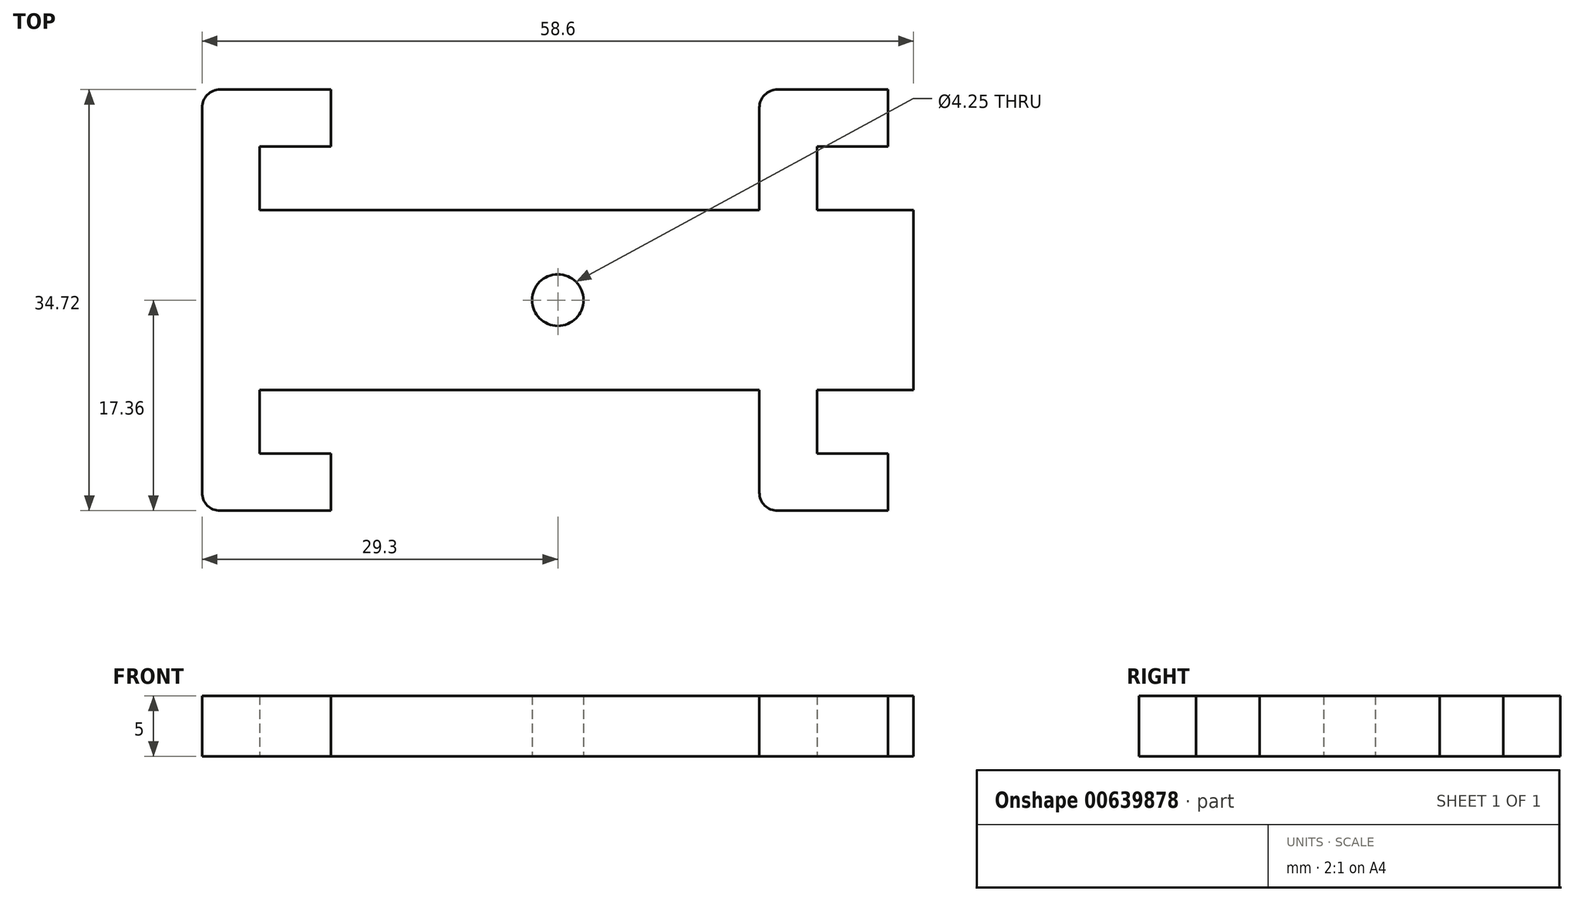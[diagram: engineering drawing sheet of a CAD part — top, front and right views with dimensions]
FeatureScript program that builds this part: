
annotation { "Feature Type Name" : "Feature", "Feature Type Description" : "" }
export const myFeature = defineFeature(function(context is Context, id is Id, definition is map)
    precondition{}
    {
        {
            var Q0;
            Q0=qCreatedBy(makeId("Top.planeOp"),FACE);
            var sketch = newSketch(context, id + "F0", { "sketchPlane" : qUnion([Q0])});
            skCircle(sketch, "E0", {"center": v(0, 0) * mm, "radius": 2.13 * mm});
            skLineSegment(sketch, "E1", {"start": v(-29.3, 0) * mm, "end": v(-29.3, 17.36) * mm});
            skLineSegment(sketch, "E2", {"start": v(-29.3, 17.36) * mm, "end": v(-18.7, 17.36) * mm});
            skLineSegment(sketch, "E3", {"start": v(-18.7, 17.36) * mm, "end": v(-18.7, 12.66) * mm});
            skLineSegment(sketch, "E4", {"start": v(-18.7, 12.66) * mm, "end": v(-24.55, 12.66) * mm});
            skLineSegment(sketch, "E5", {"start": v(-24.55, 12.66) * mm, "end": v(-24.55, 7.4) * mm});
            skLineSegment(sketch, "E6", {"start": v(-24.55, 7.4) * mm, "end": v(16.6, 7.41) * mm});
            skLineSegment(sketch, "E7", {"start": v(16.6, 7.41) * mm, "end": v(16.6, 17.36) * mm});
            skLineSegment(sketch, "E8", {"start": v(16.6, 17.36) * mm, "end": v(27.2, 17.36) * mm});
            skLineSegment(sketch, "E9", {"start": v(27.2, 17.36) * mm, "end": v(27.2, 12.66) * mm});
            skLineSegment(sketch, "E10", {"start": v(27.2, 12.66) * mm, "end": v(21.35, 12.66) * mm});
            skLineSegment(sketch, "E11", {"start": v(21.35, 12.66) * mm, "end": v(21.35, 7.41) * mm});
            skLineSegment(sketch, "E12", {"start": v(21.35, 7.4) * mm, "end": v(29.3, 7.41) * mm});
            skLineSegment(sketch, "E13", {"start": v(29.3, 7.41) * mm, "end": v(29.3, 0) * mm});
            skLineSegment(sketch, "E14", {"start": v(29.3, 0) * mm, "end": v(2.12, 0) * mm});
            skLineSegment(sketch, "E15", {"start": v(-29.3, 0) * mm, "end": v(-2.13, 0) * mm});
            skSolve(sketch);
        }
        {
            var Q0;
            Q0=makeQuery(id+"F0.imprint","IMPRINT",FACE,{"disambiguationData":[TD([[makeQuery(id+"F0.imprint","IMPRINT",EDGE,{"derivedFrom":sQuery(id+"F0.wireOp",EDGE,"E1")}),-1.0]])]});
            extrude(context, id + "F1", {"entities" : qUnion([Q0]), "depth" : 5 * mm, "offsetDistance" : 25 * mm});
        }
        {
            var Q0;
            Q0=makeQuery(id+"F1.opExtrude","SWEPT_EDGE",EDGE,{"disambiguationData":[OSD([sQuery(id+"F0.wireOp",EDGE,"E1"),sQuery(id+"F0.wireOp",EDGE,"E2")])]});
            var Q1;
            Q1=makeQuery(id+"F1.opExtrude","SWEPT_EDGE",EDGE,{"disambiguationData":[OSD([sQuery(id+"F0.wireOp",EDGE,"E7"),sQuery(id+"F0.wireOp",EDGE,"E8")])]});
            fillet(context, id + "F2", {"entities" : qUnion([Q0, Q1]), "radius" : 1.5 * mm, "tangentPropagation" : true, "allowEdgeOverflow" : false});
        }
        {
            var Q0;
            Q0=makeQuery(id+"F1.opExtrude","SWEPT_BODY",BODY,{"disambiguationData":[OSD([sQuery(id+"F0.wireOp",EDGE,"E0"),sQuery(id+"F0.wireOp",EDGE,"E1"),sQuery(id+"F0.wireOp",EDGE,"E2"),sQuery(id+"F0.wireOp",EDGE,"E3"),sQuery(id+"F0.wireOp",EDGE,"E4"),sQuery(id+"F0.wireOp",EDGE,"E5"),sQuery(id+"F0.wireOp",EDGE,"E6"),sQuery(id+"F0.wireOp",EDGE,"E7"),sQuery(id+"F0.wireOp",EDGE,"E8"),sQuery(id+"F0.wireOp",EDGE,"E9"),sQuery(id+"F0.wireOp",EDGE,"E10"),sQuery(id+"F0.wireOp",EDGE,"E11"),sQuery(id+"F0.wireOp",EDGE,"E12"),sQuery(id+"F0.wireOp",EDGE,"E13"),sQuery(id+"F0.wireOp",EDGE,"E14"),sQuery(id+"F0.wireOp",EDGE,"E15")])]});
            var Q1;
            Q1=makeQuery(id+"F1.opExtrude","SWEPT_FACE",FACE,{"disambiguationData":[OSD([sQuery(id+"F0.wireOp",EDGE,"E15")])]});
            mirror(context, id + "F3", {"operationType" : NewBodyOperationType.ADD, "entities" : qUnion([Q0]), "mirrorPlane" : qUnion([Q1])});
        }
    });
